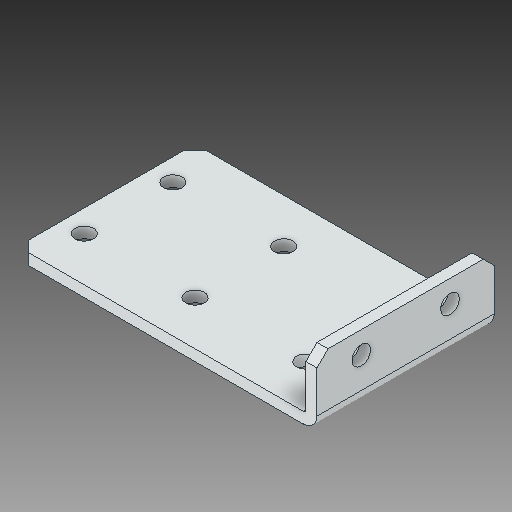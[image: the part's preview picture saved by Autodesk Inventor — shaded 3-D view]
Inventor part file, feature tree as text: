
AUTODESK INVENTOR PART (.ipt)
format: ipt  version: 2018 (Build 220112000, 112)  size: 110,592 bytes
history: native  units: in
note: dims shown in document units (in); Inventor stores cm internally (conversion verified against a paired STEP export)
features: chamfer x1
ambient origin geometry x8: Origin, YZ Plane, XZ Plane, XY Plane, X Axis, Y Axis, Z Axis, Center Point
bodies: Solid1 (feature_tree)
feature tree (1):
  chamfer  "Chamfer2"  [1 undecoded]
note: 1 required parameter value undecoded (feature->parameter linkage not recoverable at this tier; creation-order binding heuristic only, values carry confidence <= 0.55)
